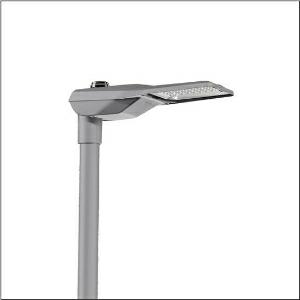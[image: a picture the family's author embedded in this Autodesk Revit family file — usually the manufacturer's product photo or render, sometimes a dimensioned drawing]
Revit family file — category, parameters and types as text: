
# Revit family: streetlight_sl_21_mini___p1_0a_5xe6a47n08hb_abf4
name_source: partatom
category: Lighting Fixtures
units: mm (PartAtom-declared; Revit-internal decimal feet)

## family parameters
Cut with Voids When Loaded = No
Host = Face
Light Source = No
Part Type = Normal
Room Calculation Point = No
Round Connector Dimension = Use Diameter
Shared = No

## types (1)
- --- (1 x LED, 9430 lm, 66 W, 4000K)
    Apparent Load = 66 VA
    CIE Flux Codes = 21 50 90 100 100
    Color Rendering = 70
    Color Temperature = 4000K
    Default Elevation = 1800 mm
    Description = Streetlight SL 21 mini, mast luminaire, primary light control with lens, of PMMA, primary optical cover: cover, of toughened safety glass, transparent, light distribution: P1.0a, light emission: direct distribution, primary light characteristic: asymmetric, installation type: side-entry, LED, 3G 1.5mm², High Power LED, rated luminous flux: 9.430lm, luminous efficacy: 143lm/W, light colour: 740, colour temperature: 4000K, control gear: NEMA (7pin), control: overheat protection, pre-setting: linear dimming characteristic, constant luminous flux control, time-dependent luminous flux control, flexible luminous flux parameterisation, mains connection: 230..240V, AC, 50/60Hz, connection cable pre-assembled, cable length: 8,5m, wiring characteristics: H07RN-F, start of lifetime: 66W, end of service life: 69W, reduction: 30W, luminaire housing, of diecast aluminium (EN AC-44300), powder-coated, Siteco® metallic grey (DB 702S), corrosivity category C5 mid according to DIN EN ISO 12944, multi-level sealing system, sealing non-destructively replaceable, inclination adjustable: 0°, 5°, 10°, 15°, length: 628mm, width: 235mm, height: 110mm, spigot size: 42mm (side-entry), mounting height: 4..8m, protection rating (complete): IP66, insulation class (complete): insulation class I (protective earthing), certification: CE, ENEC, ENEC+, VDE, impact resistance: IK09, permissible operating ambient temperature for outdoor applications: -40..+50°C, standard-compliant lighting for roads and squares, packaging unit: 1 piece

Light Distribution: P1.0a
    Height = 110 mm
    Lamp = 1 x LED
    Lamp Light Flux = 9430 lm
    Lamp Power = 66 W
    Lamp count = 1
    Length = 625 mm
    Luminous efficacy = 143 lm/W
    Manufacturer = Siteco
    ModVariant = No
    Model = 5XE6A47N08HB
    Number of Poles = 1
    OnlyDefault = Yes
    Power Factor = 1
    Product Name = Streetlight SL 21 mini | P1.0a
    Product group = mast luminaire | pylon top
    ProductGroupID = 6100
    Protection Class = Protection class I
    Protection Degree = IP 66
    RLX_Detail_Level = 1
    RLX_Emergency_Light_Flux = 0 lm
    RLX_Emergency_Type = 0
    RLX_Emergency_Type_DB = No
    RlxData = <blob elided: 103477 chars, md5=576e4ea0>
    Socket = socket
    Standby Power = 0 W
    System Light Flux = 9430 lm
    System Power = 66 W
    Type Comments = factory setting: luminous flux: 100 % | dim-lin: 254 | 670 mA
    Type Image = l_1294379.jpg
    URL = http://relux.com
    VarID = @adj_132030
    Voltage = 0 V
    Weight = 0.00 kg
    Width = 234 mm

## geometry (parser evidence)
native form markers: Blend x4, Sweep x8
no freeform markers — native parametric forms only
